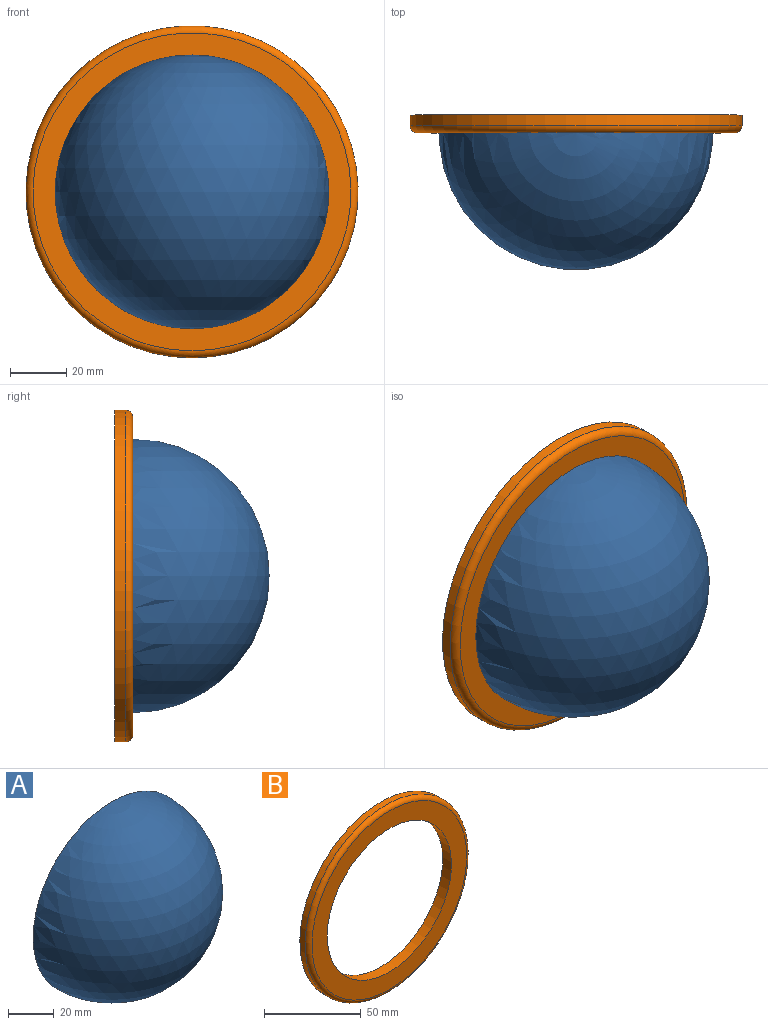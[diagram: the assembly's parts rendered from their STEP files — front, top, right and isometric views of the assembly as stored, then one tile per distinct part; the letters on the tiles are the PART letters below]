
ASSEMBLY  parts=2 mates=1
PART A: 3 faces, bbox 97.5x48.8x97.5 mm
  f0: sphere r=48.77mm, area 14943.4mm2, adj f1
  f1: plane 97.54x97.54mm, normal (0,1,0), area 977.5mm2, adj f0,f2
  f2: sphere r=45.47mm, area 12988.3mm2, adj f1
PART B: 5 faces, bbox 128.1x6.4x128.1 mm
  f0: cylinder r=45.47mm len=90.93mm, axis (0,-1,0), area 1814mm2, adj f2,f3
  f1: cylinder r=59.18mm len=118.36mm, axis (0,-1,0), area 1416.8mm2, adj f2,f4
  f2: plane 118.36x118.36mm, normal (0,1,0), area 4509.3mm2, adj f0,f1
  f3: plane 113.28x113.28mm, normal (0,-1,0), area 3585.1mm2, adj f0,f4
  f4: torus R=56.64mm, axis (0,-1,0), area 1460.5mm2, adj f1,f3
PLACE A at identity
PLACE B at identity
MATE fastened A.f1 <-> B.f0  axis (0,1,0) through (0,0,0)mm
